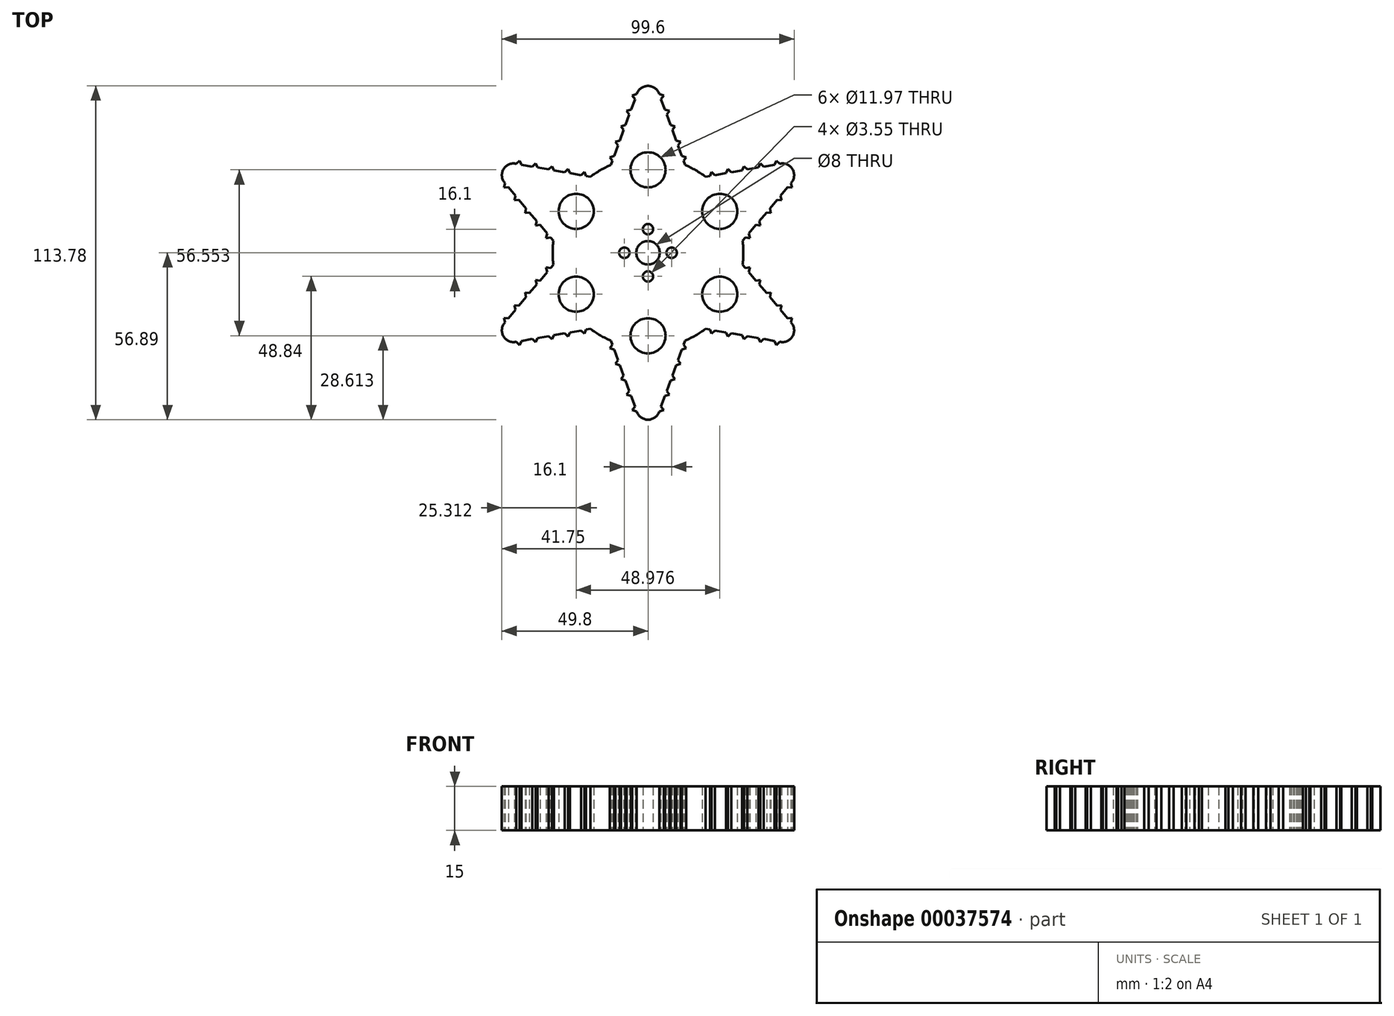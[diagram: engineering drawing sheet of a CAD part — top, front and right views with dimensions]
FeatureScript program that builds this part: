
annotation { "Feature Type Name" : "Feature", "Feature Type Description" : "" }
export const myFeature = defineFeature(function(context is Context, id is Id, definition is map)
    precondition{}
    {
        {
            var Q0;
            Q0=qCreatedBy(makeId("Top.planeOp"),FACE);
            var sketch = newSketch(context, id + "F0", { "sketchPlane" : qUnion([Q0])});
            skArc(sketch, "E0", {"start": v(-12.62, 29.95) * mm, "mid": v(-16.25, 28.15) * mm, "end": v(-19.62, 25.9) * mm});
            skPoint(sketch, "E1.visualSharp", {"position": v(0, 67.47) * mm});
            skArc(sketch, "E1.filletArc", {"start": v(3.82, 54.08) * mm, "mid": v(0, 56.89) * mm, "end": v(-3.82, 54.08) * mm});
            skArc(sketch, "E2.1.6", {"start": v(-44.93, 30.35) * mm, "mid": v(-49.27, 28.44) * mm, "end": v(-48.75, 23.74) * mm});
            skArc(sketch, "E2.2.6", {"start": v(-48.75, -23.74) * mm, "mid": v(-49.27, -28.44) * mm, "end": v(-44.93, -30.35) * mm});
            skArc(sketch, "E2.3.6", {"start": v(-3.82, -54.08) * mm, "mid": v(0, -56.89) * mm, "end": v(3.82, -54.08) * mm});
            skArc(sketch, "E2.4.6", {"start": v(44.93, -30.35) * mm, "mid": v(49.27, -28.44) * mm, "end": v(48.75, -23.74) * mm});
            skArc(sketch, "E2.5.6", {"start": v(48.75, 23.74) * mm, "mid": v(49.27, 28.44) * mm, "end": v(44.93, 30.35) * mm});
            skArc(sketch, "E3.trimOffspring", {"start": v(-32.25, 4.04) * mm, "mid": v(-32.5, 0) * mm, "end": v(-32.25, -4.04) * mm});
            skArc(sketch, "E4.trimOffspring", {"start": v(-19.62, -25.9) * mm, "mid": v(-16.25, -28.15) * mm, "end": v(-12.62, -29.95) * mm});
            skArc(sketch, "E5.trimOffspring", {"start": v(12.62, -29.95) * mm, "mid": v(16.25, -28.15) * mm, "end": v(19.62, -25.9) * mm});
            skArc(sketch, "E6.trimOffspring", {"start": v(32.25, -4.04) * mm, "mid": v(32.5, 0) * mm, "end": v(32.25, 4.04) * mm});
            skArc(sketch, "E7.trimOffspring", {"start": v(19.62, 25.9) * mm, "mid": v(16.25, 28.15) * mm, "end": v(12.62, 29.95) * mm});
            skCircle(sketch, "E8", {"center": v(0, 0) * mm, "radius": 4 * mm});
            skCircle(sketch, "E9", {"center": v(0, 28.28) * mm, "radius": 5.98 * mm});
            skCircle(sketch, "E10.1.0", {"center": v(-24.49, 14.14) * mm, "radius": 5.98 * mm});
            skCircle(sketch, "E10.2.0", {"center": v(-24.49, -14.14) * mm, "radius": 5.98 * mm});
            skCircle(sketch, "E10.3.0", {"center": v(0, -28.28) * mm, "radius": 5.98 * mm});
            skCircle(sketch, "E10.4.0", {"center": v(24.49, -14.14) * mm, "radius": 5.98 * mm});
            skCircle(sketch, "E10.5.0", {"center": v(24.49, 14.14) * mm, "radius": 5.98 * mm});
            skCircle(sketch, "E11", {"center": v(0, 8.05) * mm, "radius": 1.77 * mm});
            skCircle(sketch, "E12.1.0", {"center": v(-8.05, 0) * mm, "radius": 1.77 * mm});
            skCircle(sketch, "E12.2.0", {"center": v(0, -8.05) * mm, "radius": 1.77 * mm});
            skCircle(sketch, "E12.3.0", {"center": v(8.05, 0) * mm, "radius": 1.77 * mm});
            skLineSegment(sketch, "E13", {"start": v(4.44, -52.39) * mm, "end": v(5.74, -48.82) * mm});
            skLineSegment(sketch, "E14", {"start": v(-12.62, -29.95) * mm, "end": v(-12.11, -31.35) * mm});
            skLineSegment(sketch, "E15", {"start": v(-19.62, -25.9) * mm, "end": v(-21.09, -26.16) * mm});
            skLineSegment(sketch, "E16", {"start": v(-47.59, -22.35) * mm, "end": v(-45.15, -19.44) * mm});
            skLineSegment(sketch, "E17", {"start": v(-32.25, 4.04) * mm, "end": v(-33.2, 5.18) * mm});
            skLineSegment(sketch, "E18", {"start": v(-43.15, 30.04) * mm, "end": v(-39.4, 29.38) * mm});
            skLineSegment(sketch, "E19", {"start": v(-12.62, 29.95) * mm, "end": v(-12.11, 31.35) * mm});
            skLineSegment(sketch, "E20", {"start": v(4.44, 52.39) * mm, "end": v(5.74, 48.82) * mm});
            skLineSegment(sketch, "E21", {"start": v(19.62, 25.9) * mm, "end": v(21.09, 26.16) * mm});
            skLineSegment(sketch, "E22", {"start": v(47.59, 22.35) * mm, "end": v(45.15, 19.44) * mm});
            skLineSegment(sketch, "E23", {"start": v(32.25, -4.04) * mm, "end": v(33.2, -5.18) * mm});
            skLineSegment(sketch, "E24", {"start": v(43.15, -30.04) * mm, "end": v(39.4, -29.38) * mm});
            skLineSegment(sketch, "E25", {"start": v(3.82, -54.08) * mm, "end": v(5.35, -53.6) * mm});
            skLineSegment(sketch, "E26", {"start": v(5.35, -53.6) * mm, "end": v(4.44, -52.39) * mm});
            skLineSegment(sketch, "E27.1.0.0", {"start": v(7.27, -48.34) * mm, "end": v(6.36, -47.13) * mm});
            skLineSegment(sketch, "E27.1.0.1", {"start": v(5.74, -48.82) * mm, "end": v(7.27, -48.34) * mm});
            skLineSegment(sketch, "E27.2.0.0", {"start": v(9.18, -43.08) * mm, "end": v(8.27, -41.87) * mm});
            skLineSegment(sketch, "E27.2.0.1", {"start": v(7.66, -43.56) * mm, "end": v(9.18, -43.08) * mm});
            skLineSegment(sketch, "E27.3.0.0", {"start": v(11.1, -37.82) * mm, "end": v(10.2, -36.6) * mm});
            skLineSegment(sketch, "E27.3.0.1", {"start": v(9.58, -38.3) * mm, "end": v(11.1, -37.82) * mm});
            skLineSegment(sketch, "E27.4.0.0", {"start": v(13.02, -32.56) * mm, "end": v(12.11, -31.35) * mm});
            skLineSegment(sketch, "E27.4.0.1", {"start": v(11.5, -33.03) * mm, "end": v(13.02, -32.56) * mm});
            skLineSegment(sketch, "E27.direction1", {"start": v(5.35, -53.6) * mm, "end": v(7.27, -48.34) * mm, "construction": true});
            skLineSegment(sketch, "E28.trimOffspring", {"start": v(6.36, -47.13) * mm, "end": v(7.66, -43.56) * mm});
            skLineSegment(sketch, "E29.trimOffspring", {"start": v(8.27, -41.87) * mm, "end": v(9.58, -38.3) * mm});
            skLineSegment(sketch, "E30.trimOffspring", {"start": v(10.2, -36.6) * mm, "end": v(11.5, -33.03) * mm});
            skLineSegment(sketch, "E31.trimOffspring", {"start": v(12.11, -31.35) * mm, "end": v(12.62, -29.95) * mm});
            skLineSegment(sketch, "E32.MirrorCS", {"start": v(-13.02, -32.56) * mm, "end": v(-12.11, -31.35) * mm});
            skLineSegment(sketch, "E33.MirrorCS", {"start": v(-5.35, -53.6) * mm, "end": v(-4.44, -52.39) * mm});
            skLineSegment(sketch, "E34.MirrorCS", {"start": v(-3.82, -54.08) * mm, "end": v(-5.35, -53.6) * mm});
            skLineSegment(sketch, "E35.MirrorCS", {"start": v(-11.5, -33.03) * mm, "end": v(-13.02, -32.56) * mm});
            skLineSegment(sketch, "E36.MirrorCS", {"start": v(-11.1, -37.82) * mm, "end": v(-10.2, -36.6) * mm});
            skLineSegment(sketch, "E37.MirrorCS", {"start": v(-9.58, -38.3) * mm, "end": v(-11.1, -37.82) * mm});
            skLineSegment(sketch, "E38.MirrorCS", {"start": v(-9.18, -43.08) * mm, "end": v(-8.27, -41.87) * mm});
            skLineSegment(sketch, "E39.MirrorCS", {"start": v(-7.66, -43.56) * mm, "end": v(-9.18, -43.08) * mm});
            skLineSegment(sketch, "E40.MirrorCS", {"start": v(-7.27, -48.34) * mm, "end": v(-6.36, -47.13) * mm});
            skLineSegment(sketch, "E41.MirrorCS", {"start": v(-5.74, -48.82) * mm, "end": v(-7.27, -48.34) * mm});
            skLineSegment(sketch, "E42.trimOffspring", {"start": v(-11.5, -33.03) * mm, "end": v(-10.2, -36.6) * mm});
            skLineSegment(sketch, "E43.trimOffspring", {"start": v(-9.58, -38.3) * mm, "end": v(-8.27, -41.87) * mm});
            skLineSegment(sketch, "E44.trimOffspring", {"start": v(-7.66, -43.56) * mm, "end": v(-6.36, -47.13) * mm});
            skLineSegment(sketch, "E45.trimOffspring", {"start": v(-5.74, -48.82) * mm, "end": v(-4.44, -52.39) * mm});
            skLineSegment(sketch, "E46.1.0", {"start": v(34.7, -5) * mm, "end": v(33.2, -5.18) * mm});
            skLineSegment(sketch, "E46.1.1", {"start": v(34.35, -6.56) * mm, "end": v(34.7, -5) * mm});
            skLineSegment(sketch, "E46.1.2", {"start": v(38.3, -9.3) * mm, "end": v(36.8, -9.47) * mm});
            skLineSegment(sketch, "E46.1.3", {"start": v(37.95, -10.85) * mm, "end": v(38.3, -9.3) * mm});
            skLineSegment(sketch, "E46.1.4", {"start": v(41.9, -13.59) * mm, "end": v(40.4, -13.77) * mm});
            skLineSegment(sketch, "E46.1.5", {"start": v(41.55, -15.15) * mm, "end": v(41.9, -13.59) * mm});
            skLineSegment(sketch, "E46.1.6", {"start": v(45.5, -17.88) * mm, "end": v(44, -18.06) * mm});
            skLineSegment(sketch, "E46.1.7", {"start": v(45.15, -19.44) * mm, "end": v(45.5, -17.88) * mm});
            skLineSegment(sketch, "E46.1.8", {"start": v(49.1, -22.17) * mm, "end": v(47.59, -22.35) * mm});
            skLineSegment(sketch, "E46.1.9", {"start": v(48.75, -23.74) * mm, "end": v(49.1, -22.17) * mm});
            skLineSegment(sketch, "E46.1.10", {"start": v(44.93, -30.35) * mm, "end": v(43.75, -31.43) * mm});
            skLineSegment(sketch, "E46.1.11", {"start": v(43.75, -31.43) * mm, "end": v(43.15, -30.04) * mm});
            skLineSegment(sketch, "E46.1.12", {"start": v(39.4, -29.38) * mm, "end": v(38.23, -30.46) * mm});
            skLineSegment(sketch, "E46.1.13", {"start": v(38.23, -30.46) * mm, "end": v(37.64, -29.07) * mm});
            skLineSegment(sketch, "E46.1.14", {"start": v(33.9, -28.41) * mm, "end": v(32.72, -29.5) * mm});
            skLineSegment(sketch, "E46.1.15", {"start": v(32.72, -29.5) * mm, "end": v(32.12, -28.1) * mm});
            skLineSegment(sketch, "E46.1.16", {"start": v(28.37, -27.44) * mm, "end": v(27.2, -28.52) * mm});
            skLineSegment(sketch, "E46.1.17", {"start": v(27.2, -28.52) * mm, "end": v(26.6, -27.13) * mm});
            skLineSegment(sketch, "E46.1.18", {"start": v(22.85, -26.47) * mm, "end": v(21.68, -27.55) * mm});
            skLineSegment(sketch, "E46.1.19", {"start": v(21.68, -27.55) * mm, "end": v(21.09, -26.16) * mm});
            skLineSegment(sketch, "E46.2.0", {"start": v(21.68, 27.55) * mm, "end": v(21.09, 26.16) * mm});
            skLineSegment(sketch, "E46.2.1", {"start": v(22.85, 26.47) * mm, "end": v(21.68, 27.55) * mm});
            skLineSegment(sketch, "E46.2.2", {"start": v(27.2, 28.52) * mm, "end": v(26.6, 27.13) * mm});
            skLineSegment(sketch, "E46.2.3", {"start": v(28.37, 27.44) * mm, "end": v(27.2, 28.52) * mm});
            skLineSegment(sketch, "E46.2.4", {"start": v(32.72, 29.5) * mm, "end": v(32.12, 28.1) * mm});
            skLineSegment(sketch, "E46.2.5", {"start": v(33.9, 28.41) * mm, "end": v(32.72, 29.5) * mm});
            skLineSegment(sketch, "E46.2.6", {"start": v(38.23, 30.46) * mm, "end": v(37.64, 29.07) * mm});
            skLineSegment(sketch, "E46.2.7", {"start": v(39.4, 29.38) * mm, "end": v(38.23, 30.46) * mm});
            skLineSegment(sketch, "E46.2.8", {"start": v(43.75, 31.43) * mm, "end": v(43.15, 30.04) * mm});
            skLineSegment(sketch, "E46.2.9", {"start": v(44.93, 30.35) * mm, "end": v(43.75, 31.43) * mm});
            skLineSegment(sketch, "E46.2.10", {"start": v(48.75, 23.74) * mm, "end": v(49.1, 22.17) * mm});
            skLineSegment(sketch, "E46.2.11", {"start": v(49.1, 22.17) * mm, "end": v(47.59, 22.35) * mm});
            skLineSegment(sketch, "E46.2.12", {"start": v(45.15, 19.44) * mm, "end": v(45.5, 17.88) * mm});
            skLineSegment(sketch, "E46.2.13", {"start": v(45.5, 17.88) * mm, "end": v(44, 18.06) * mm});
            skLineSegment(sketch, "E46.2.14", {"start": v(41.55, 15.15) * mm, "end": v(41.9, 13.59) * mm});
            skLineSegment(sketch, "E46.2.15", {"start": v(41.9, 13.59) * mm, "end": v(40.4, 13.77) * mm});
            skLineSegment(sketch, "E46.2.16", {"start": v(37.95, 10.85) * mm, "end": v(38.3, 9.3) * mm});
            skLineSegment(sketch, "E46.2.17", {"start": v(38.3, 9.3) * mm, "end": v(36.8, 9.47) * mm});
            skLineSegment(sketch, "E46.2.18", {"start": v(34.35, 6.56) * mm, "end": v(34.7, 5) * mm});
            skLineSegment(sketch, "E46.2.19", {"start": v(34.7, 5) * mm, "end": v(33.2, 5.18) * mm});
            skLineSegment(sketch, "E46.3.0", {"start": v(-13.02, 32.56) * mm, "end": v(-12.11, 31.35) * mm});
            skLineSegment(sketch, "E46.3.1", {"start": v(-11.5, 33.03) * mm, "end": v(-13.02, 32.56) * mm});
            skLineSegment(sketch, "E46.3.2", {"start": v(-11.1, 37.82) * mm, "end": v(-10.2, 36.6) * mm});
            skLineSegment(sketch, "E46.3.3", {"start": v(-9.58, 38.3) * mm, "end": v(-11.1, 37.82) * mm});
            skLineSegment(sketch, "E46.3.4", {"start": v(-9.18, 43.08) * mm, "end": v(-8.27, 41.87) * mm});
            skLineSegment(sketch, "E46.3.5", {"start": v(-7.66, 43.56) * mm, "end": v(-9.18, 43.08) * mm});
            skLineSegment(sketch, "E46.3.6", {"start": v(-7.27, 48.34) * mm, "end": v(-6.36, 47.13) * mm});
            skLineSegment(sketch, "E46.3.7", {"start": v(-5.74, 48.82) * mm, "end": v(-7.27, 48.34) * mm});
            skLineSegment(sketch, "E46.3.8", {"start": v(-5.35, 53.6) * mm, "end": v(-4.44, 52.39) * mm});
            skLineSegment(sketch, "E46.3.9", {"start": v(-3.82, 54.08) * mm, "end": v(-5.35, 53.6) * mm});
            skLineSegment(sketch, "E46.3.10", {"start": v(3.82, 54.08) * mm, "end": v(5.35, 53.6) * mm});
            skLineSegment(sketch, "E46.3.11", {"start": v(5.35, 53.6) * mm, "end": v(4.44, 52.39) * mm});
            skLineSegment(sketch, "E46.3.12", {"start": v(5.74, 48.82) * mm, "end": v(7.27, 48.34) * mm});
            skLineSegment(sketch, "E46.3.13", {"start": v(7.27, 48.34) * mm, "end": v(6.36, 47.13) * mm});
            skLineSegment(sketch, "E46.3.14", {"start": v(7.66, 43.56) * mm, "end": v(9.18, 43.08) * mm});
            skLineSegment(sketch, "E46.3.15", {"start": v(9.18, 43.08) * mm, "end": v(8.27, 41.87) * mm});
            skLineSegment(sketch, "E46.3.16", {"start": v(9.58, 38.3) * mm, "end": v(11.1, 37.82) * mm});
            skLineSegment(sketch, "E46.3.17", {"start": v(11.1, 37.82) * mm, "end": v(10.2, 36.6) * mm});
            skLineSegment(sketch, "E46.3.18", {"start": v(11.5, 33.03) * mm, "end": v(13.02, 32.56) * mm});
            skLineSegment(sketch, "E46.3.19", {"start": v(13.02, 32.56) * mm, "end": v(12.11, 31.35) * mm});
            skLineSegment(sketch, "E46.4.0", {"start": v(-34.7, 5) * mm, "end": v(-33.2, 5.18) * mm});
            skLineSegment(sketch, "E46.4.1", {"start": v(-34.35, 6.56) * mm, "end": v(-34.7, 5) * mm});
            skLineSegment(sketch, "E46.4.2", {"start": v(-38.3, 9.3) * mm, "end": v(-36.8, 9.47) * mm});
            skLineSegment(sketch, "E46.4.3", {"start": v(-37.95, 10.85) * mm, "end": v(-38.3, 9.3) * mm});
            skLineSegment(sketch, "E46.4.4", {"start": v(-41.9, 13.59) * mm, "end": v(-40.4, 13.77) * mm});
            skLineSegment(sketch, "E46.4.5", {"start": v(-41.55, 15.15) * mm, "end": v(-41.9, 13.59) * mm});
            skLineSegment(sketch, "E46.4.6", {"start": v(-45.5, 17.88) * mm, "end": v(-44, 18.06) * mm});
            skLineSegment(sketch, "E46.4.7", {"start": v(-45.15, 19.44) * mm, "end": v(-45.5, 17.88) * mm});
            skLineSegment(sketch, "E46.4.8", {"start": v(-49.1, 22.17) * mm, "end": v(-47.59, 22.35) * mm});
            skLineSegment(sketch, "E46.4.9", {"start": v(-48.75, 23.74) * mm, "end": v(-49.1, 22.17) * mm});
            skLineSegment(sketch, "E46.4.10", {"start": v(-44.93, 30.35) * mm, "end": v(-43.75, 31.43) * mm});
            skLineSegment(sketch, "E46.4.11", {"start": v(-43.75, 31.43) * mm, "end": v(-43.15, 30.04) * mm});
            skLineSegment(sketch, "E46.4.12", {"start": v(-39.4, 29.38) * mm, "end": v(-38.23, 30.46) * mm});
            skLineSegment(sketch, "E46.4.13", {"start": v(-38.23, 30.46) * mm, "end": v(-37.64, 29.07) * mm});
            skLineSegment(sketch, "E46.4.14", {"start": v(-33.9, 28.41) * mm, "end": v(-32.72, 29.5) * mm});
            skLineSegment(sketch, "E46.4.15", {"start": v(-32.72, 29.5) * mm, "end": v(-32.12, 28.1) * mm});
            skLineSegment(sketch, "E46.4.16", {"start": v(-28.37, 27.44) * mm, "end": v(-27.2, 28.52) * mm});
            skLineSegment(sketch, "E46.4.17", {"start": v(-27.2, 28.52) * mm, "end": v(-26.6, 27.13) * mm});
            skLineSegment(sketch, "E46.4.18", {"start": v(-22.85, 26.47) * mm, "end": v(-21.68, 27.55) * mm});
            skLineSegment(sketch, "E46.4.19", {"start": v(-21.68, 27.55) * mm, "end": v(-21.09, 26.16) * mm});
            skLineSegment(sketch, "E46.5.0", {"start": v(-21.68, -27.55) * mm, "end": v(-21.09, -26.16) * mm});
            skLineSegment(sketch, "E46.5.1", {"start": v(-22.85, -26.47) * mm, "end": v(-21.68, -27.55) * mm});
            skLineSegment(sketch, "E46.5.2", {"start": v(-27.2, -28.52) * mm, "end": v(-26.6, -27.13) * mm});
            skLineSegment(sketch, "E46.5.3", {"start": v(-28.37, -27.44) * mm, "end": v(-27.2, -28.52) * mm});
            skLineSegment(sketch, "E46.5.4", {"start": v(-32.72, -29.5) * mm, "end": v(-32.12, -28.1) * mm});
            skLineSegment(sketch, "E46.5.5", {"start": v(-33.9, -28.41) * mm, "end": v(-32.72, -29.5) * mm});
            skLineSegment(sketch, "E46.5.6", {"start": v(-38.23, -30.46) * mm, "end": v(-37.64, -29.07) * mm});
            skLineSegment(sketch, "E46.5.7", {"start": v(-39.4, -29.38) * mm, "end": v(-38.23, -30.46) * mm});
            skLineSegment(sketch, "E46.5.8", {"start": v(-43.75, -31.43) * mm, "end": v(-43.15, -30.04) * mm});
            skLineSegment(sketch, "E46.5.9", {"start": v(-44.93, -30.35) * mm, "end": v(-43.75, -31.43) * mm});
            skLineSegment(sketch, "E46.5.10", {"start": v(-48.75, -23.74) * mm, "end": v(-49.1, -22.17) * mm});
            skLineSegment(sketch, "E46.5.11", {"start": v(-49.1, -22.17) * mm, "end": v(-47.59, -22.35) * mm});
            skLineSegment(sketch, "E46.5.12", {"start": v(-45.15, -19.44) * mm, "end": v(-45.5, -17.88) * mm});
            skLineSegment(sketch, "E46.5.13", {"start": v(-45.5, -17.88) * mm, "end": v(-44, -18.06) * mm});
            skLineSegment(sketch, "E46.5.14", {"start": v(-41.55, -15.15) * mm, "end": v(-41.9, -13.59) * mm});
            skLineSegment(sketch, "E46.5.15", {"start": v(-41.9, -13.59) * mm, "end": v(-40.4, -13.77) * mm});
            skLineSegment(sketch, "E46.5.16", {"start": v(-37.95, -10.85) * mm, "end": v(-38.3, -9.3) * mm});
            skLineSegment(sketch, "E46.5.17", {"start": v(-38.3, -9.3) * mm, "end": v(-36.8, -9.47) * mm});
            skLineSegment(sketch, "E46.5.18", {"start": v(-34.35, -6.56) * mm, "end": v(-34.7, -5) * mm});
            skLineSegment(sketch, "E46.5.19", {"start": v(-34.7, -5) * mm, "end": v(-33.2, -5.18) * mm});
            skLineSegment(sketch, "E47.trimOffspring", {"start": v(-39.4, -29.38) * mm, "end": v(-43.15, -30.04) * mm});
            skLineSegment(sketch, "E48.trimOffspring", {"start": v(-33.9, -28.41) * mm, "end": v(-37.64, -29.07) * mm});
            skLineSegment(sketch, "E49.trimOffspring", {"start": v(-28.37, -27.44) * mm, "end": v(-32.12, -28.1) * mm});
            skLineSegment(sketch, "E50.trimOffspring", {"start": v(-22.85, -26.47) * mm, "end": v(-26.6, -27.13) * mm});
            skLineSegment(sketch, "E51.trimOffspring", {"start": v(-44, -18.06) * mm, "end": v(-41.55, -15.15) * mm});
            skLineSegment(sketch, "E52.trimOffspring", {"start": v(-40.4, -13.77) * mm, "end": v(-37.95, -10.85) * mm});
            skLineSegment(sketch, "E53.trimOffspring", {"start": v(-36.8, -9.47) * mm, "end": v(-34.35, -6.56) * mm});
            skLineSegment(sketch, "E54.trimOffspring", {"start": v(-33.2, -5.18) * mm, "end": v(-32.25, -4.04) * mm});
            skLineSegment(sketch, "E55.trimOffspring", {"start": v(-34.35, 6.56) * mm, "end": v(-36.8, 9.47) * mm});
            skLineSegment(sketch, "E56.trimOffspring", {"start": v(-37.95, 10.85) * mm, "end": v(-40.4, 13.77) * mm});
            skLineSegment(sketch, "E57.trimOffspring", {"start": v(-41.55, 15.15) * mm, "end": v(-44, 18.06) * mm});
            skLineSegment(sketch, "E58.trimOffspring", {"start": v(-45.15, 19.44) * mm, "end": v(-47.59, 22.35) * mm});
            skLineSegment(sketch, "E59.trimOffspring", {"start": v(-37.64, 29.07) * mm, "end": v(-33.9, 28.41) * mm});
            skLineSegment(sketch, "E60.trimOffspring", {"start": v(-32.12, 28.1) * mm, "end": v(-28.37, 27.44) * mm});
            skLineSegment(sketch, "E61.trimOffspring", {"start": v(-26.6, 27.13) * mm, "end": v(-22.85, 26.47) * mm});
            skLineSegment(sketch, "E62.trimOffspring", {"start": v(-21.09, 26.16) * mm, "end": v(-19.62, 25.9) * mm});
            skLineSegment(sketch, "E63.trimOffspring", {"start": v(-5.74, 48.82) * mm, "end": v(-4.44, 52.39) * mm});
            skLineSegment(sketch, "E64.trimOffspring", {"start": v(-7.66, 43.56) * mm, "end": v(-6.36, 47.13) * mm});
            skLineSegment(sketch, "E65.trimOffspring", {"start": v(-9.58, 38.3) * mm, "end": v(-8.27, 41.87) * mm});
            skLineSegment(sketch, "E66.trimOffspring", {"start": v(-11.5, 33.03) * mm, "end": v(-10.2, 36.6) * mm});
            skLineSegment(sketch, "E67.trimOffspring", {"start": v(6.36, 47.13) * mm, "end": v(7.66, 43.56) * mm});
            skLineSegment(sketch, "E68.trimOffspring", {"start": v(8.27, 41.87) * mm, "end": v(9.58, 38.3) * mm});
            skLineSegment(sketch, "E69.trimOffspring", {"start": v(10.2, 36.6) * mm, "end": v(11.5, 33.03) * mm});
            skLineSegment(sketch, "E70.trimOffspring", {"start": v(12.11, 31.35) * mm, "end": v(12.62, 29.95) * mm});
            skLineSegment(sketch, "E71.trimOffspring", {"start": v(22.85, 26.47) * mm, "end": v(26.6, 27.13) * mm});
            skLineSegment(sketch, "E72.trimOffspring", {"start": v(28.37, 27.44) * mm, "end": v(32.12, 28.1) * mm});
            skLineSegment(sketch, "E73.trimOffspring", {"start": v(33.9, 28.41) * mm, "end": v(37.64, 29.07) * mm});
            skLineSegment(sketch, "E74.trimOffspring", {"start": v(39.4, 29.38) * mm, "end": v(43.15, 30.04) * mm});
            skLineSegment(sketch, "E75.trimOffspring", {"start": v(33.2, 5.18) * mm, "end": v(32.25, 4.04) * mm});
            skLineSegment(sketch, "E76.trimOffspring", {"start": v(36.8, 9.47) * mm, "end": v(34.35, 6.56) * mm});
            skLineSegment(sketch, "E77.trimOffspring", {"start": v(40.4, 13.77) * mm, "end": v(37.95, 10.85) * mm});
            skLineSegment(sketch, "E78.trimOffspring", {"start": v(44, 18.06) * mm, "end": v(41.55, 15.15) * mm});
            skLineSegment(sketch, "E79.trimOffspring", {"start": v(21.09, -26.16) * mm, "end": v(19.62, -25.9) * mm});
            skLineSegment(sketch, "E80.trimOffspring", {"start": v(26.6, -27.13) * mm, "end": v(22.85, -26.47) * mm});
            skLineSegment(sketch, "E81.trimOffspring", {"start": v(32.12, -28.1) * mm, "end": v(28.37, -27.44) * mm});
            skLineSegment(sketch, "E82.trimOffspring", {"start": v(37.64, -29.07) * mm, "end": v(33.9, -28.41) * mm});
            skLineSegment(sketch, "E83.trimOffspring", {"start": v(45.15, -19.44) * mm, "end": v(47.59, -22.35) * mm});
            skLineSegment(sketch, "E84.trimOffspring", {"start": v(41.55, -15.15) * mm, "end": v(44, -18.06) * mm});
            skLineSegment(sketch, "E85.trimOffspring", {"start": v(37.95, -10.85) * mm, "end": v(40.4, -13.77) * mm});
            skLineSegment(sketch, "E86.trimOffspring", {"start": v(34.35, -6.56) * mm, "end": v(36.8, -9.47) * mm});
            skSolve(sketch);
        }
        {
            var Q0;
            Q0=qSketchRegion(id+"F0",true);
            extrude(context, id + "F1", {"entities" : qUnion([Q0]), "depth" : 15 * mm});
        }
    });
